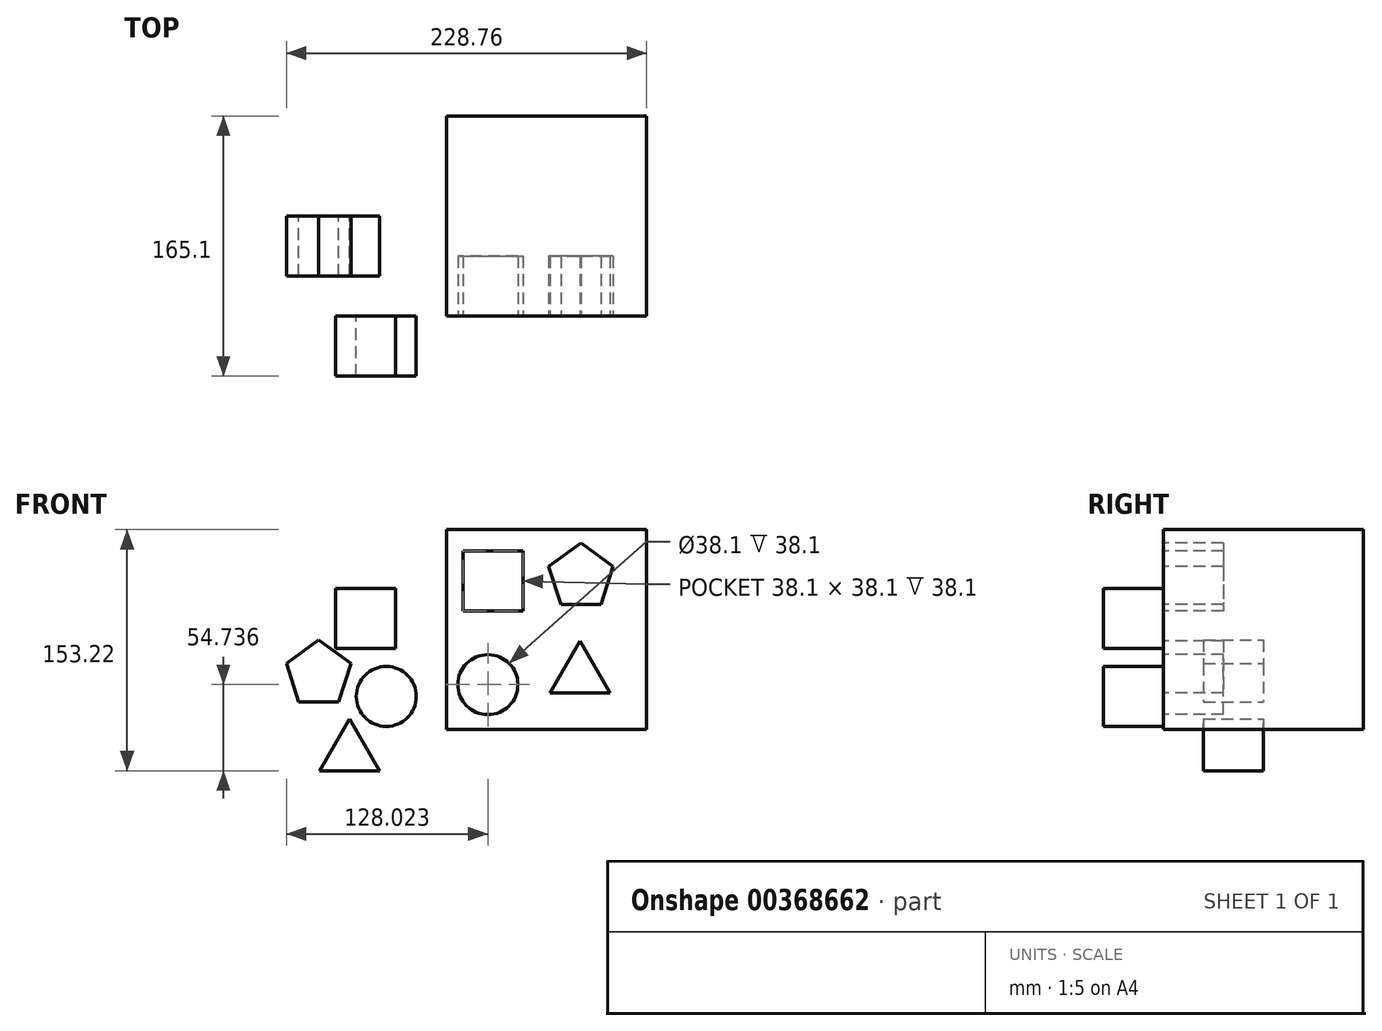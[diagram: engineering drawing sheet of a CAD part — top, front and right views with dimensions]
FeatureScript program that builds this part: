
annotation { "Feature Type Name" : "Feature", "Feature Type Description" : "" }
export const myFeature = defineFeature(function(context is Context, id is Id, definition is map)
    precondition{}
    {
        {
            var Q0;
            Q0=qCreatedBy(makeId("Front.planeOp"),FACE);
            var sketch = newSketch(context, id + "F0", { "sketchPlane" : qUnion([Q0])});
            skLineSegment(sketch, "E0.bottom", {"start": v(-55.67, 71.75) * mm, "end": v(71.33, 71.75) * mm});
            skLineSegment(sketch, "E0.top", {"start": v(-55.67, -55.25) * mm, "end": v(71.33, -55.25) * mm});
            skLineSegment(sketch, "E0.left", {"start": v(-55.67, 71.75) * mm, "end": v(-55.67, -55.25) * mm});
            skLineSegment(sketch, "E0.right", {"start": v(71.33, 71.75) * mm, "end": v(71.33, -55.25) * mm});
            skSolve(sketch);
        }
        {
            var Q0;
            Q0 = qSketchRegion(id + "F0", true);
            extrude(context, id + "F1", {"entities" : qUnion([Q0]), "endBound" : BoundingType.SYMMETRIC, "depth" : 127 * mm});
        }
        {
            var Q0;
            Q0=makeQuery(id+"F1.opExtrude","CAP_FACE",FACE,{"disambiguationData":[OSD([sQuery(id+"F0.wireOp",EDGE,"E0.bottom"),sQuery(id+"F0.wireOp",EDGE,"E0.top"),sQuery(id+"F0.wireOp",EDGE,"E0.left"),sQuery(id+"F0.wireOp",EDGE,"E0.right")])],"isStart":false});
            var sketch = newSketch(context, id + "F2", { "sketchPlane" : qUnion([Q0])});
            skLineSegment(sketch, "E1.bottom", {"start": v(-45.21, 58.15) * mm, "end": v(-7.11, 58.15) * mm});
            skLineSegment(sketch, "E1.top", {"start": v(-45.21, 20.05) * mm, "end": v(-7.11, 20.05) * mm});
            skLineSegment(sketch, "E1.left", {"start": v(-45.21, 58.15) * mm, "end": v(-45.21, 20.05) * mm});
            skLineSegment(sketch, "E1.right", {"start": v(-7.11, 58.15) * mm, "end": v(-7.11, 20.05) * mm});
            skSolve(sketch);
        }
        {
            var Q0;
            Q0 = qSketchRegion(id + "F2", true);
            extrude(context, id + "F3", {"entities" : qUnion([Q0]), "operationType" : NewBodyOperationType.REMOVE, "oppositeDirection" : true, "depth" : 38.1 * mm});
        }
        {
            var Q0;
            Q0=makeQuery(id+"F1.opExtrude","CAP_FACE",FACE,{"disambiguationData":[OSD([sQuery(id+"F0.wireOp",EDGE,"E0.bottom"),sQuery(id+"F0.wireOp",EDGE,"E0.top"),sQuery(id+"F0.wireOp",EDGE,"E0.left"),sQuery(id+"F0.wireOp",EDGE,"E0.right")])],"isStart":false});
            var sketch = newSketch(context, id + "F4", { "sketchPlane" : qUnion([Q0])});
            skCircle(sketch, "E2.cCircle", {"center": v(29.6, 41.74) * mm, "radius": 17.48 * mm, "construction": true});
            skLineSegment(sketch, "E2.0", {"start": v(42.3, 24.26) * mm, "end": v(16.9, 24.26) * mm});
            skLineSegment(sketch, "E2.1", {"start": v(16.9, 24.26) * mm, "end": v(9.05, 48.42) * mm});
            skLineSegment(sketch, "E2.2", {"start": v(9.05, 48.42) * mm, "end": v(29.6, 63.35) * mm});
            skLineSegment(sketch, "E2.3", {"start": v(29.6, 63.35) * mm, "end": v(50.15, 48.42) * mm});
            skLineSegment(sketch, "E2.4", {"start": v(50.15, 48.42) * mm, "end": v(42.3, 24.26) * mm});
            skPoint(sketch, "E2.0.midPoint", {"position": v(29.6, 24.26) * mm});
            skSolve(sketch);
        }
        {
            var Q0;
            Q0 = qSketchRegion(id + "F4", true);
            extrude(context, id + "F5", {"entities" : qUnion([Q0]), "operationType" : NewBodyOperationType.REMOVE, "oppositeDirection" : true, "depth" : 38.1 * mm});
        }
        {
            var Q0;
            Q0=makeQuery(id+"F1.opExtrude","CAP_FACE",FACE,{"disambiguationData":[OSD([sQuery(id+"F0.wireOp",EDGE,"E0.bottom"),sQuery(id+"F0.wireOp",EDGE,"E0.top"),sQuery(id+"F0.wireOp",EDGE,"E0.left"),sQuery(id+"F0.wireOp",EDGE,"E0.right")])],"isStart":false});
            var sketch = newSketch(context, id + "F6", { "sketchPlane" : qUnion([Q0])});
            skCircle(sketch, "E3.cCircle", {"center": v(29.22, -20.87) * mm, "radius": 11 * mm, "construction": true});
            skLineSegment(sketch, "E3.0", {"start": v(48.27, -31.87) * mm, "end": v(10.17, -31.87) * mm});
            skLineSegment(sketch, "E3.1", {"start": v(10.17, -31.87) * mm, "end": v(29.22, 1.13) * mm});
            skLineSegment(sketch, "E3.2", {"start": v(29.22, 1.13) * mm, "end": v(48.27, -31.87) * mm});
            skPoint(sketch, "E3.0.midPoint", {"position": v(29.22, -31.87) * mm});
            skSolve(sketch);
        }
        {
            var Q0;
            Q0 = qSketchRegion(id + "F6", true);
            extrude(context, id + "F7", {"entities" : qUnion([Q0]), "operationType" : NewBodyOperationType.REMOVE, "oppositeDirection" : true, "depth" : 38.1 * mm});
        }
        {
            var Q0;
            Q0=makeQuery(id+"F1.opExtrude","CAP_FACE",FACE,{"disambiguationData":[OSD([sQuery(id+"F0.wireOp",EDGE,"E0.bottom"),sQuery(id+"F0.wireOp",EDGE,"E0.top"),sQuery(id+"F0.wireOp",EDGE,"E0.left"),sQuery(id+"F0.wireOp",EDGE,"E0.right")])],"isStart":false});
            var sketch = newSketch(context, id + "F8", { "sketchPlane" : qUnion([Q0])});
            skCircle(sketch, "E4", {"center": v(-29.4, -26.73) * mm, "radius": 19.05 * mm});
            skSolve(sketch);
        }
        {
            var Q0;
            Q0 = qSketchRegion(id + "F8", true);
            extrude(context, id + "F9", {"entities" : qUnion([Q0]), "operationType" : NewBodyOperationType.REMOVE, "oppositeDirection" : true, "depth" : 38.1 * mm});
        }
        {
            var Q0;
            Q0=makeQuery(id+"F1.opExtrude","CAP_FACE",FACE,{"disambiguationData":[OSD([sQuery(id+"F0.wireOp",EDGE,"E0.bottom"),sQuery(id+"F0.wireOp",EDGE,"E0.top"),sQuery(id+"F0.wireOp",EDGE,"E0.left"),sQuery(id+"F0.wireOp",EDGE,"E0.right")])],"isStart":false});
            var sketch = newSketch(context, id + "F10", { "sketchPlane" : qUnion([Q0])});
            skLineSegment(sketch, "E5.bottom", {"start": v(-126.18, 34.4) * mm, "end": v(-88.08, 34.4) * mm});
            skLineSegment(sketch, "E5.top", {"start": v(-126.18, -3.7) * mm, "end": v(-88.08, -3.7) * mm});
            skLineSegment(sketch, "E5.left", {"start": v(-126.18, 34.4) * mm, "end": v(-126.18, -3.7) * mm});
            skLineSegment(sketch, "E5.right", {"start": v(-88.08, 34.4) * mm, "end": v(-88.08, -3.7) * mm});
            skSolve(sketch);
        }
        {
            var Q0;
            Q0 = qSketchRegion(id + "F10", true);
            extrude(context, id + "F11", {"entities" : qUnion([Q0]), "depth" : 38.1 * mm});
        }
        {
            var Q0;
            Q0=qCreatedBy(makeId("Front.planeOp"),FACE);
            var sketch = newSketch(context, id + "F12", { "sketchPlane" : qUnion([Q0])});
            skCircle(sketch, "E6.cCircle", {"center": v(-136.88, -20.11) * mm, "radius": 17.48 * mm, "construction": true});
            skLineSegment(sketch, "E6.0", {"start": v(-124.18, -37.6) * mm, "end": v(-149.58, -37.6) * mm});
            skLineSegment(sketch, "E6.1", {"start": v(-149.58, -37.6) * mm, "end": v(-157.43, -13.44) * mm});
            skLineSegment(sketch, "E6.2", {"start": v(-157.43, -13.44) * mm, "end": v(-136.88, 1.5) * mm});
            skLineSegment(sketch, "E6.3", {"start": v(-136.88, 1.5) * mm, "end": v(-116.33, -13.44) * mm});
            skLineSegment(sketch, "E6.4", {"start": v(-116.33, -13.44) * mm, "end": v(-124.18, -37.6) * mm});
            skPoint(sketch, "E6.0.midPoint", {"position": v(-136.88, -37.6) * mm});
            skSolve(sketch);
        }
        {
            var Q0;
            Q0 = qSketchRegion(id + "F12", true);
            extrude(context, id + "F13", {"entities" : qUnion([Q0]), "depth" : 38.1 * mm});
        }
        {
            var Q0;
            Q0=qCreatedBy(makeId("Front.planeOp"),FACE);
            var sketch = newSketch(context, id + "F14", { "sketchPlane" : qUnion([Q0])});
            skCircle(sketch, "E7.cCircle", {"center": v(-117.33, -70.47) * mm, "radius": 11 * mm, "construction": true});
            skLineSegment(sketch, "E7.0", {"start": v(-136.38, -81.47) * mm, "end": v(-117.33, -48.47) * mm});
            skLineSegment(sketch, "E7.1", {"start": v(-117.33, -48.47) * mm, "end": v(-98.28, -81.47) * mm});
            skLineSegment(sketch, "E7.2", {"start": v(-98.28, -81.47) * mm, "end": v(-136.38, -81.47) * mm});
            skPoint(sketch, "E7.0.midPoint", {"position": v(-126.85, -64.97) * mm});
            skSolve(sketch);
        }
        {
            var Q0;
            Q0=makeQuery(id+"F14.imprint","IMPRINT",FACE,{"disambiguationData":[TD([[makeQuery(id+"F14.imprint","IMPRINT",EDGE,{"derivedFrom":sQuery(id+"F14.wireOp",EDGE,"E7.0")}),-1.0]])]});
            extrude(context, id + "F15", {"entities" : qUnion([Q0]), "depth" : 38.1 * mm});
        }
        {
            var Q0;
            Q0=makeQuery(id+"F1.opExtrude","CAP_FACE",FACE,{"disambiguationData":[OSD([sQuery(id+"F0.wireOp",EDGE,"E0.bottom"),sQuery(id+"F0.wireOp",EDGE,"E0.top"),sQuery(id+"F0.wireOp",EDGE,"E0.left"),sQuery(id+"F0.wireOp",EDGE,"E0.right")])],"isStart":false});
            var sketch = newSketch(context, id + "F16", { "sketchPlane" : qUnion([Q0])});
            skCircle(sketch, "E8", {"center": v(-93.97, -34.26) * mm, "radius": 19.05 * mm});
            skSolve(sketch);
        }
        {
            var Q0;
            Q0 = qSketchRegion(id + "F16", true);
            extrude(context, id + "F17", {"entities" : qUnion([Q0]), "depth" : 38.1 * mm});
        }
    });
